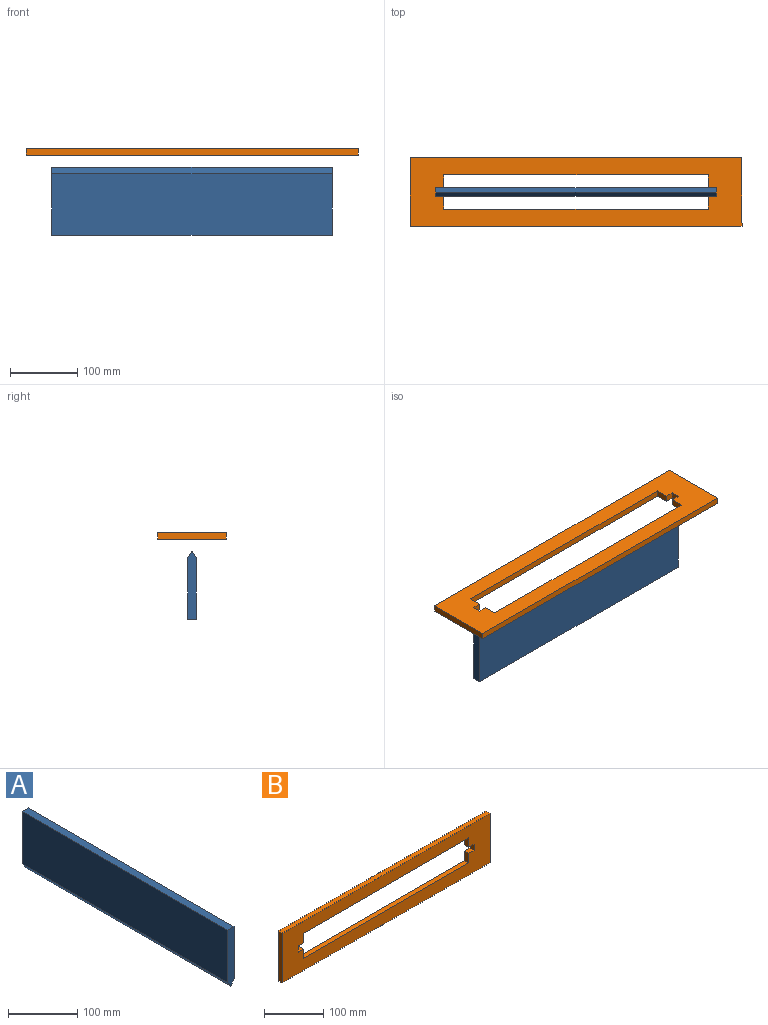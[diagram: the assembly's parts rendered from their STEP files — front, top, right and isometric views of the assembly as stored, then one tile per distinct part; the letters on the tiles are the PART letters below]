
ASSEMBLY  parts=2 mates=1
PART A: 7 faces, bbox 12.7x419.1x101.6 mm
  f0: plane 419.1x92.08mm, normal (1,0,0), area 38588.6mm2, adj f1,f4,f5,f6
  f1: plane 419.1x12.7mm, normal (0,0,1), area 5322.6mm2, adj f0,f2,f5,f6
  f2: plane 419.1x92.08mm, normal (-1,0,0), area 38588.6mm2, adj f1,f3,f5,f6
  f3: plane 419.1x9.53mm, normal (-0.83,0,-0.55), area 4797.7mm2, adj f2,f4,f5,f6
  f4: plane 419.1x9.53mm, normal (0.83,0,-0.55), area 4797.7mm2, adj f0,f3,f5,f6
  f5: plane 101.6x12.7mm, normal (0,-1,0), area 1229.8mm2, adj f0,f1,f2,f3,f4
  f6: plane 101.6x12.7mm, normal (0,1,0), area 1229.8mm2, adj f0,f1,f2,f3,f4
PART B: 18 faces, bbox 495.3x9.5x101.6 mm
  f0: plane 495.3x9.53mm, normal (0,0,-1), area 4717.7mm2, adj f1,f15,f16,f17
  f1: plane 101.6x9.53mm, normal (1,0,0), area 967.7mm2, adj f0,f2,f16,f17
  f2: plane 495.3x9.53mm, normal (0,0,1), area 4717.7mm2, adj f1,f15,f16,f17
  f3: plane 19.3x9.53mm, normal (1,0,0), area 183.9mm2, adj f4,f14,f16,f17
  f4: plane 12.45x9.53mm, normal (0,0,1), area 118.5mm2, adj f3,f5,f16,f17
  f5: plane 12.7x9.53mm, normal (1,0,0), area 121mm2, adj f4,f6,f16,f17
  f6: plane 12.45x9.53mm, normal (0,0,-1), area 118.5mm2, adj f5,f7,f16,f17
  f7: plane 19.3x9.53mm, normal (1,0,0), area 183.9mm2, adj f6,f8,f16,f17
  f8: plane 394.21x9.53mm, normal (0,0,-1), area 3754.8mm2, adj f7,f9,f16,f17
  f9: plane 19.3x9.53mm, normal (-1,0,0), area 183.9mm2, adj f8,f10,f16,f17
  f10: plane 12.45x9.53mm, normal (0,0,-1), area 118.5mm2, adj f9,f11,f16,f17
  f11: plane 12.7x9.53mm, normal (-1,0,0), area 121mm2, adj f10,f12,f16,f17
  f12: plane 12.45x9.53mm, normal (0,0,1), area 118.5mm2, adj f11,f13,f16,f17
  f13: plane 19.3x9.53mm, normal (-1,0,0), area 183.9mm2, adj f12,f14,f16,f17
  f14: plane 394.21x9.53mm, normal (0,0,1), area 3754.8mm2, adj f3,f13,f16,f17
  f15: plane 101.6x9.53mm, normal (-1,0,0), area 967.7mm2, adj f0,f2,f16,f17
  f16: plane 495.3x101.6mm, normal (0,-1,0), area 29780.3mm2, adj f0,f1,f2,f3,f4,f5,f6,f7
  f17: plane 495.3x101.6mm, normal (0,1,0), area 29780.3mm2, adj f0,f1,f2,f3,f4,f5,f6,f7
PLACE A rot(axis=(0.71,0.71,0),180deg) t=(-251,43.12,-137.17)mm
PLACE B rot(axis=(1,0,0),90deg) t=(-460.55,43.12,-58.72)mm
MATE slider B.f16 <-> A.f1  axis (0,0,-1) through (-460.55,43.12,-68.25)mm
